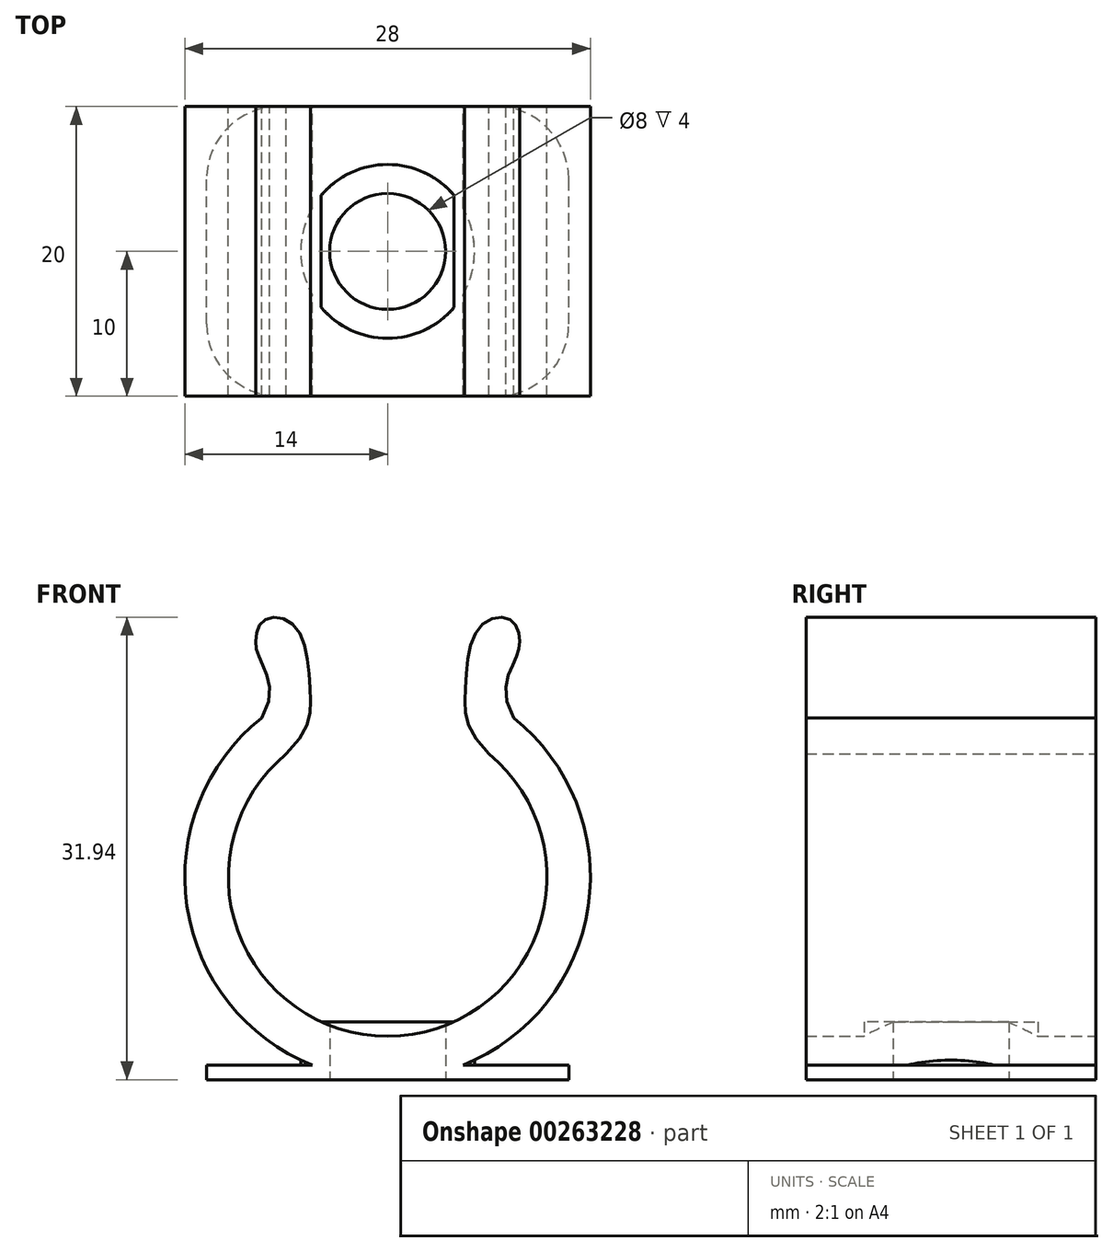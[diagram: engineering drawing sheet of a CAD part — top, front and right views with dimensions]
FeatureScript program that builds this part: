
annotation { "Feature Type Name" : "Feature", "Feature Type Description" : "" }
export const myFeature = defineFeature(function(context is Context, id is Id, definition is map)
    precondition{}
    {
        {
            var Q0;
            Q0=qCreatedBy(makeId("Front.planeOp"),FACE);
            var sketch = newSketch(context, id + "F0", { "sketchPlane" : qUnion([Q0])});
            skArc(sketch, "E0", {"start": v(-7, 22.49) * mm, "mid": v(0, 3) * mm, "end": v(7, 22.49) * mm});
            skLineSegment(sketch, "E1.MirrorCS", {"start": v(7, 41.76) * mm, "end": v(7, 1.73) * mm, "construction": true});
            skPoint(sketch, "E2", {"position": v(-7, 22.49) * mm});
            skPoint(sketch, "E3", {"position": v(7, 22.49) * mm});
            skArc(sketch, "E4.0", {"start": v(-8.7, 24.97) * mm, "mid": v(0, 0) * mm, "end": v(8.7, 24.97) * mm});
            skPoint(sketch, "E5.middle", {"position": v(0, 0) * mm});
            skLineSegment(sketch, "E6", {"start": v(-12.5, 0) * mm, "end": v(12.5, 0) * mm});
            skLineSegment(sketch, "E7", {"start": v(-12.5, 1) * mm, "end": v(-12.5, 0) * mm});
            skLineSegment(sketch, "E8", {"start": v(-12.5, 1) * mm, "end": v(12.5, 1) * mm});
            skLineSegment(sketch, "E9", {"start": v(12.5, 1) * mm, "end": v(12.5, 0) * mm});
            skPoint(sketch, "E10", {"position": v(-8.7, 24.97) * mm});
            skPoint(sketch, "E11", {"position": v(8.7, 24.97) * mm});
            skLineSegment(sketch, "E12", {"start": v(0, 14) * mm, "end": v(0, 36.21) * mm, "construction": true});
            skFitSpline(sketch, "E13", {"points": [v(-7, 22.49) * mm, v(-5.37, 26.96) * mm, v(-6.35, 31.25) * mm, v(-8.42, 31.8) * mm, v(-9.12, 30.42) * mm, v(-8.77, 28.94) * mm, v(-8.7, 24.97) * mm], "startDerivative": vector(25.9, 26.37) * mm, "endDerivative": vector(-16.66, -28.75) * mm});
            skFitSpline(sketch, "E14.MirrorCS", {"points": [v(7, 22.49) * mm, v(5.37, 26.96) * mm, v(6.35, 31.25) * mm, v(8.42, 31.8) * mm, v(9.12, 30.42) * mm, v(8.77, 28.94) * mm, v(8.7, 24.97) * mm], "startDerivative": vector(-25.9, 26.37) * mm, "endDerivative": vector(16.66, -28.75) * mm});
            skLineSegment(sketch, "E15", {"start": v(-5.51, 34.26) * mm, "end": v(-5.51, 17.93) * mm, "construction": true});
            skSolve(sketch);
        }
        {
            var Q0;
            Q0=qSketchRegion(id+"F0",true);
            extrude(context, id + "F1", {"entities" : qUnion([Q0]), "endBound" : BoundingType.SYMMETRIC, "depth" : 20 * mm});
        }
        {
            var Q0;
            Q0=makeQuery(id+"F1.opExtrude","SWEPT_FACE",FACE,{"disambiguationData":[OSD([sQuery(id+"F0.wireOp",EDGE,"E6")])]});
            var sketch = newSketch(context, id + "F2", { "sketchPlane" : qUnion([Q0])});
            skCircle(sketch, "E16", {"center": v(0, 0) * mm, "radius": 6 * mm});
            skSolve(sketch);
        }
        {
            var Q0;
            Q0=makeQuery(id+"F2.imprint","IMPRINT",FACE,{"disambiguationData":[TD([[makeQuery(id+"F2.imprint","IMPRINT",EDGE,{"derivedFrom":sQuery(id+"F2.wireOp",EDGE,"E16")}),1.0]])]});
            var Q1;
            Q1=sQuery(id+"F2.wireOp",EDGE,"E16");
            extrude(context, id + "F3", {"entities" : qUnion([Q0]), "operationType" : NewBodyOperationType.ADD, "surfaceEntities" : qUnion([Q1]), "oppositeDirection" : true, "depth" : 4 * mm});
        }
        {
            var Q0;
            Q0=makeQuery(id+"F1.opExtrude","SWEPT_FACE",FACE,{"disambiguationData":[OSD([sQuery(id+"F0.wireOp",EDGE,"E6")])]});
            var sketch = newSketch(context, id + "F4", { "sketchPlane" : qUnion([Q0])});
            skCircle(sketch, "E17", {"center": v(0, 0) * mm, "radius": 4 * mm});
            skSolve(sketch);
        }
        {
            var Q0;
            Q0=qSketchRegion(id+"F4",true);
            extrude(context, id + "F5", {"entities" : qUnion([Q0]), "operationType" : NewBodyOperationType.REMOVE, "oppositeDirection" : true, "depth" : 10 * mm});
        }
        {
            var Q0;
            Q0=makeQuery(id+"F1.opExtrude","CAP_EDGE",EDGE,{"disambiguationData":[OSD([sQuery(id+"F0.wireOp",EDGE,"E9")])],"isStart":false});
            var Q1;
            Q1=makeQuery(id+"F1.opExtrude","CAP_EDGE",EDGE,{"disambiguationData":[OSD([sQuery(id+"F0.wireOp",EDGE,"E9")])],"isStart":true});
            var Q2;
            Q2=makeQuery(id+"F1.opExtrude","CAP_EDGE",EDGE,{"disambiguationData":[OSD([sQuery(id+"F0.wireOp",EDGE,"E7")])],"isStart":true});
            var Q3;
            Q3=makeQuery(id+"F1.opExtrude","CAP_EDGE",EDGE,{"disambiguationData":[OSD([sQuery(id+"F0.wireOp",EDGE,"E7")])],"isStart":false});
            fillet(context, id + "F6", {"entities" : qUnion([Q0, Q1, Q2, Q3]), "radius" : 5 * mm, "tangentPropagation" : true, "allowEdgeOverflow" : false});
        }
    });
